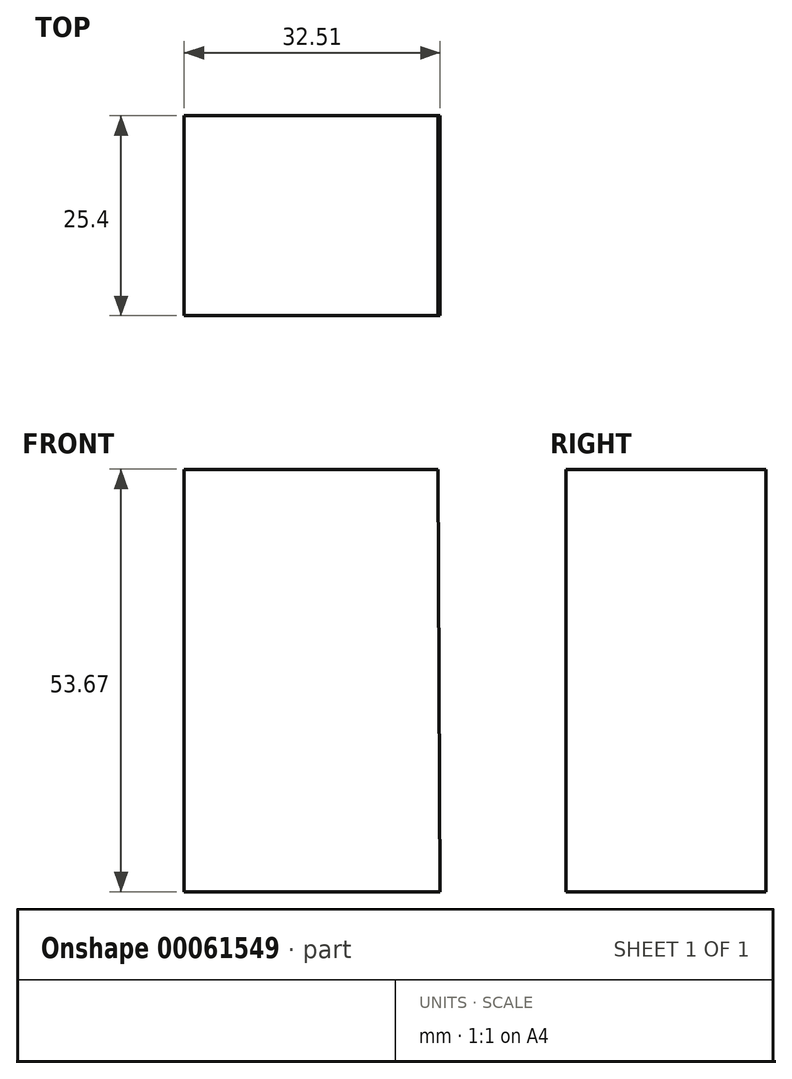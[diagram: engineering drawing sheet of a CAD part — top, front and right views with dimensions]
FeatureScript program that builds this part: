
annotation { "Feature Type Name" : "Feature", "Feature Type Description" : "" }
export const myFeature = defineFeature(function(context is Context, id is Id, definition is map)
    precondition{}
    {
        {
            var Q0;
            Q0=qCreatedBy(makeId("Front.planeOp"),FACE);
            var sketch = newSketch(context, id + "F0", { "sketchPlane" : qUnion([Q0])});
            skLineSegment(sketch, "E0", {"start": v(17.38, 53.67) * mm, "end": v(-14.85, 53.67) * mm});
            skLineSegment(sketch, "E1", {"start": v(-14.85, 53.67) * mm, "end": v(-14.85, 0) * mm});
            skLineSegment(sketch, "E2", {"start": v(-14.85, 0) * mm, "end": v(17.66, 0) * mm});
            skLineSegment(sketch, "E3", {"start": v(17.66, 0) * mm, "end": v(17.38, 53.67) * mm});
            skLineSegment(sketch, "E4", {"start": v(0, 0) * mm, "end": v(17.38, -20.88) * mm});
            skLineSegment(sketch, "E5", {"start": v(17.38, -20.88) * mm, "end": v(17.66, 0) * mm});
            skSolve(sketch);
        }
        {
            var Q0;
            Q0=makeQuery(id+"F0.imprint","IMPRINT",FACE,{"disambiguationData":[TD([[makeQuery(id+"F0.imprint","IMPRINT",EDGE,{"derivedFrom":sQuery(id+"F0.wireOp",EDGE,"E0")}),1.0]])]});
            extrude(context, id + "F1", {"entities" : qUnion([Q0]), "depth" : 25.4 * mm});
        }
    });
